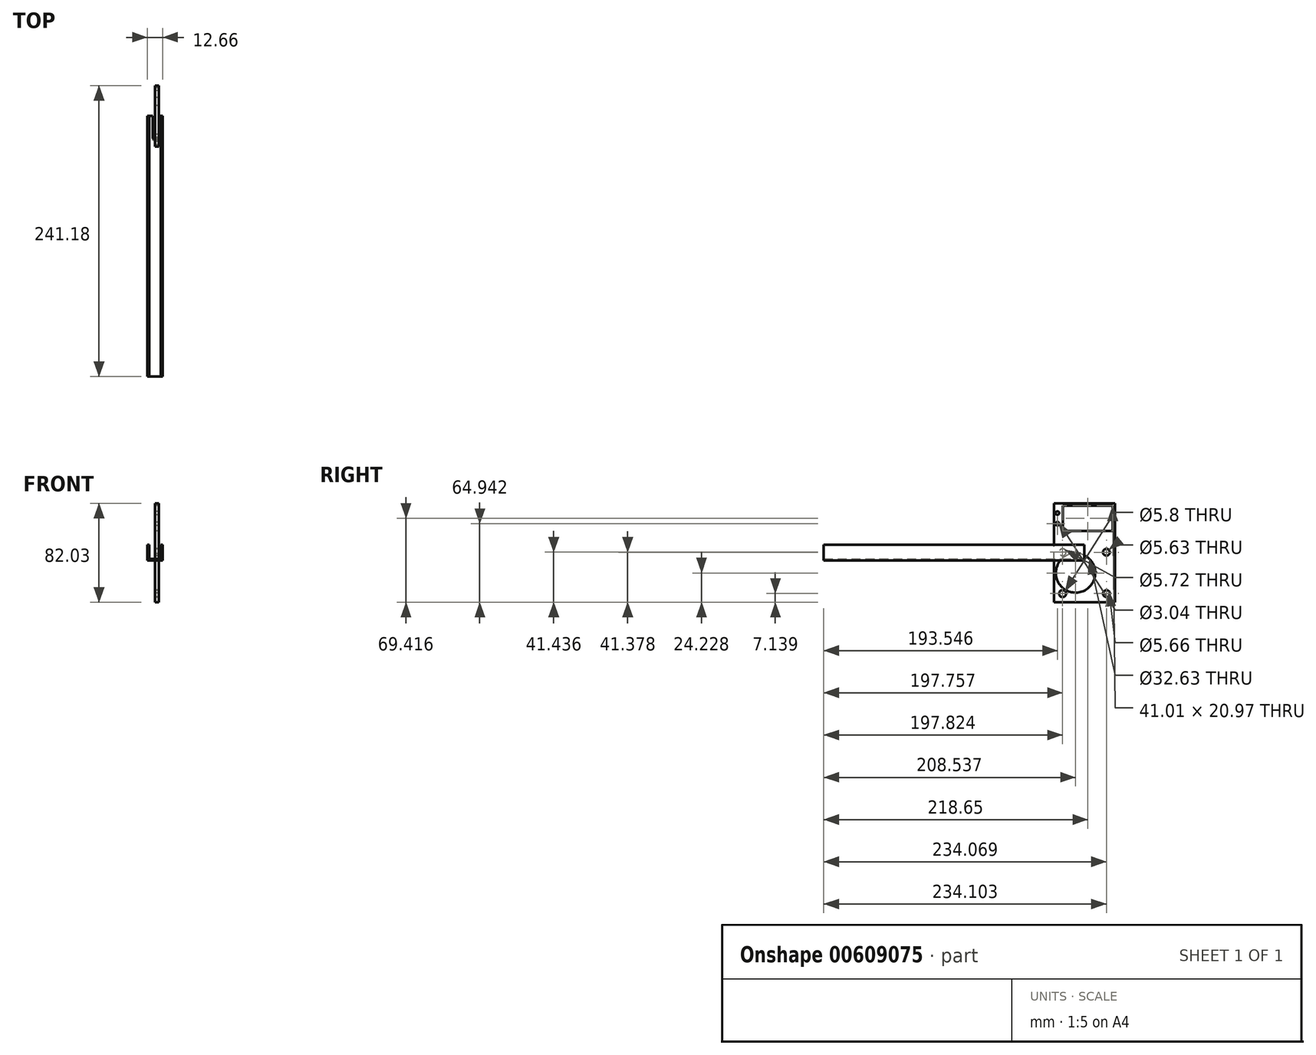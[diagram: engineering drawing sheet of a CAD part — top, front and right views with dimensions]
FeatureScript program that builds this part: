
annotation { "Feature Type Name" : "Feature", "Feature Type Description" : "" }
export const myFeature = defineFeature(function(context is Context, id is Id, definition is map)
    precondition{}
    {
        {
            var Q0;
            Q0=qCreatedBy(makeId("Front.planeOp"),FACE);
            var sketch = newSketch(context, id + "F0", { "sketchPlane" : qUnion([Q0])});
            skLineSegment(sketch, "E0.bottom", {"start": v(-6.32, 6.5) * mm, "end": v(6.33, 6.5) * mm});
            skLineSegment(sketch, "E0.top", {"start": v(-6.33, -6.5) * mm, "end": v(6.33, -6.5) * mm});
            skLineSegment(sketch, "E0.left", {"start": v(-6.32, 6.5) * mm, "end": v(-6.33, -6.5) * mm});
            skLineSegment(sketch, "E0.right", {"start": v(6.33, 6.5) * mm, "end": v(6.33, -6.5) * mm});
            skPoint(sketch, "E0.middle", {"position": v(0, 0) * mm});
            skLineSegment(sketch, "E1.bottom", {"start": v(-4.82, 6.5) * mm, "end": v(4.83, 6.5) * mm});
            skLineSegment(sketch, "E1.top", {"start": v(-4.82, -5) * mm, "end": v(4.83, -5) * mm});
            skLineSegment(sketch, "E1.left", {"start": v(-4.82, 6.5) * mm, "end": v(-4.82, -5) * mm});
            skLineSegment(sketch, "E1.right", {"start": v(4.83, 6.5) * mm, "end": v(4.83, -5) * mm});
            skSolve(sketch);
        }
        {
            var Q0;
            Q0=makeQuery(id+"F0.imprint","IMPRINT",FACE,{"disambiguationData":[TD([[makeQuery(id+"F0.imprint","IMPRINT",EDGE,{"derivedFrom":sQuery(id+"F0.wireOp",EDGE,"E0.top")}),1.0]])]});
            extrude(context, id + "F1", {"entities" : qUnion([Q0]), "depth" : 215.9 * mm, "offsetDistance" : 25 * mm});
        }
        {
            var Q0;
            Q0=qCreatedBy(makeId("Right.planeOp"),FACE);
            var sketch = newSketch(context, id + "F2", { "sketchPlane" : qUnion([Q0])});
            skCircle(sketch, "E2", {"center": v(-22.35, 32.84) * mm, "radius": 1.45 * mm});
            skPoint(sketch, "E2.first.point", {"position": v(-23.8, 33) * mm});
            skPoint(sketch, "E2.second.point", {"position": v(-20.9, 32.87) * mm});
            skPoint(sketch, "E2.third.point", {"position": v(-22.32, 31.38) * mm});
            skCircle(sketch, "E3", {"center": v(-22.35, 23.93) * mm, "radius": 1.52 * mm});
            skPoint(sketch, "E3.first.point", {"position": v(-23.86, 23.78) * mm});
            skPoint(sketch, "E3.second.point", {"position": v(-20.84, 23.91) * mm});
            skPoint(sketch, "E3.third.point", {"position": v(-22.11, 22.43) * mm});
            skCircle(sketch, "E4", {"center": v(-18.08, 0.43) * mm, "radius": 2.86 * mm});
            skPoint(sketch, "E4.first.point", {"position": v(-20.9, 0) * mm});
            skPoint(sketch, "E4.second.point", {"position": v(-15.25, 0) * mm});
            skPoint(sketch, "E4.third.point", {"position": v(-17.67, -2.4) * mm});
            skCircle(sketch, "E5", {"center": v(18.17, 0.37) * mm, "radius": 2.82 * mm});
            skPoint(sketch, "E5.first.point", {"position": v(15.38, 0) * mm});
            skPoint(sketch, "E5.second.point", {"position": v(20.96, 0) * mm});
            skPoint(sketch, "E5.third.point", {"position": v(18.67, -2.4) * mm});
            skCircle(sketch, "E6", {"center": v(-18.14, -33.87) * mm, "radius": 2.9 * mm});
            skPoint(sketch, "E6.first.point", {"position": v(-17.67, -36.73) * mm});
            skPoint(sketch, "E6.second.point", {"position": v(-17.67, -31.01) * mm});
            skPoint(sketch, "E6.third.point", {"position": v(-15.25, -34.04) * mm});
            skCircle(sketch, "E7", {"center": v(18.2, -33.87) * mm, "radius": 2.83 * mm});
            skPoint(sketch, "E7.first.point", {"position": v(15.38, -34.04) * mm});
            skPoint(sketch, "E7.second.point", {"position": v(21.03, -34.04) * mm});
            skPoint(sketch, "E7.third.point", {"position": v(18.67, -36.66) * mm});
            skLineSegment(sketch, "E8.bottom", {"start": v(-17.76, 38.9) * mm, "end": v(23.26, 38.9) * mm});
            skLineSegment(sketch, "E8.top", {"start": v(-17.76, 17.92) * mm, "end": v(23.26, 17.92) * mm});
            skLineSegment(sketch, "E8.left", {"start": v(-17.76, 38.9) * mm, "end": v(-17.76, 17.92) * mm});
            skLineSegment(sketch, "E8.right", {"start": v(23.26, 38.9) * mm, "end": v(23.26, 17.92) * mm});
            skLineSegment(sketch, "E9.bottom", {"start": v(-25.23, -41.01) * mm, "end": v(25.28, -41.01) * mm});
            skLineSegment(sketch, "E9.top", {"start": v(-25.23, 41.02) * mm, "end": v(25.28, 41.02) * mm});
            skLineSegment(sketch, "E9.left", {"start": v(-25.23, -41.01) * mm, "end": v(-25.23, 41.02) * mm});
            skLineSegment(sketch, "E9.right", {"start": v(25.28, -41.01) * mm, "end": v(25.28, 41.02) * mm});
            skSolve(sketch);
        }
        {
            var Q0;
            Q0=makeQuery(id+"F2.imprint","IMPRINT",FACE,{"disambiguationData":[TD([[makeQuery(id+"F2.imprint","IMPRINT",EDGE,{"derivedFrom":sQuery(id+"F2.wireOp",EDGE,"E2")}),-1.0]])]});
            extrude(context, id + "F3", {"entities" : qUnion([Q0]), "depth" : 3.06 * mm, "offsetDistance" : 25 * mm});
        }
        {
            var Q0;
            Q0=makeQuery(id+"F1.opExtrude","SWEPT_FACE",FACE,{"disambiguationData":[OSD([sQuery(id+"F0.wireOp",EDGE,"E0.right")])]});
            var sketch = newSketch(context, id + "F4", { "sketchPlane" : qUnion([Q0])});
            skCircle(sketch, "E10", {"center": v(-15, 0) * mm, "radius": 2.81 * mm});
            skCircle(sketch, "E11", {"center": v(-51.35, 0) * mm, "radius": 2.81 * mm});
            skCircle(sketch, "E12", {"center": v(-200.9, 0) * mm, "radius": 2.81 * mm});
            skCircle(sketch, "E13", {"center": v(-164.55, 0) * mm, "radius": 2.81 * mm});
            skSolve(sketch);
        }
        {
            var Q0;
            Q0=makeQuery(id+"F3.opExtrude","CAP_FACE",FACE,{"disambiguationData":[OSD([sQuery(id+"F2.wireOp",EDGE,"E2"),sQuery(id+"F2.wireOp",EDGE,"E3"),sQuery(id+"F2.wireOp",EDGE,"E4"),sQuery(id+"F2.wireOp",EDGE,"E5"),sQuery(id+"F2.wireOp",EDGE,"E6"),sQuery(id+"F2.wireOp",EDGE,"E7"),sQuery(id+"F2.wireOp",EDGE,"E8.bottom"),sQuery(id+"F2.wireOp",EDGE,"E8.top"),sQuery(id+"F2.wireOp",EDGE,"E8.left"),sQuery(id+"F2.wireOp",EDGE,"E8.right"),sQuery(id+"F2.wireOp",EDGE,"E9.bottom"),sQuery(id+"F2.wireOp",EDGE,"E9.top"),sQuery(id+"F2.wireOp",EDGE,"E9.left"),sQuery(id+"F2.wireOp",EDGE,"E9.right")])],"isStart":false});
            var sketch = newSketch(context, id + "F5", { "sketchPlane" : qUnion([Q0])});
            skCircle(sketch, "E14", {"center": v(-7.36, -16.78) * mm, "radius": 16.31 * mm});
            skPoint(sketch, "E14.first.point", {"position": v(-23.67, -17.19) * mm});
            skPoint(sketch, "E14.second.point", {"position": v(8.95, -16.83) * mm});
            skPoint(sketch, "E14.third.point", {"position": v(-6.2, -33.06) * mm});
            skSolve(sketch);
        }
        {
            var Q0;
            Q0=makeQuery(id+"F5.imprint","IMPRINT",FACE,{"disambiguationData":[TD([[makeQuery(id+"F5.imprint","IMPRINT",EDGE,{"derivedFrom":sQuery(id+"F5.wireOp",EDGE,"E14")}),1.0]])]});
            extrude(context, id + "F6", {"entities" : qUnion([Q0]), "operationType" : NewBodyOperationType.REMOVE, "oppositeDirection" : true, "depth" : 5 * mm, "offsetDistance" : 25 * mm});
        }
    });
